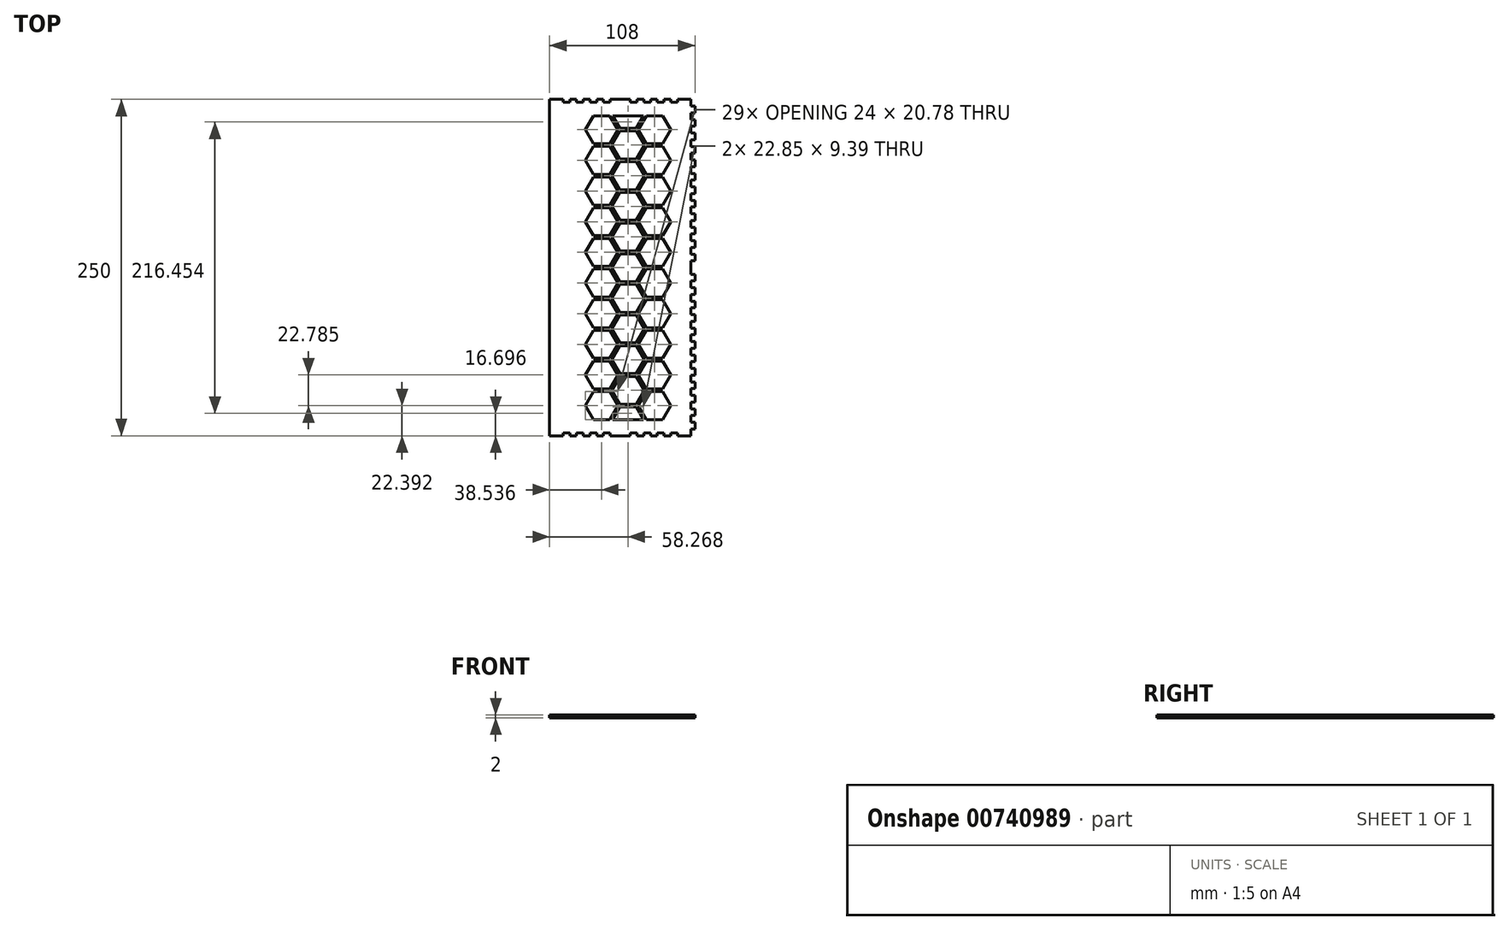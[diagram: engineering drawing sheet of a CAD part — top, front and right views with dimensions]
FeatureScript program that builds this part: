
annotation { "Feature Type Name" : "Feature", "Feature Type Description" : "" }
export const myFeature = defineFeature(function(context is Context, id is Id, definition is map)
    precondition{}
    {
        {
            var Q0;
            Q0=qCreatedBy(makeId("Top.planeOp"),FACE);
            var sketch = newSketch(context, id + "F0", { "sketchPlane" : qUnion([Q0])});
            skLineSegment(sketch, "E0.bottom", {"start": v(-52.5, 125) * mm, "end": v(-42.5, 125) * mm});
            skLineSegment(sketch, "E0.top", {"start": v(-52.5, -125) * mm, "end": v(-42.5, -125) * mm});
            skLineSegment(sketch, "E0.left", {"start": v(-52.5, 125) * mm, "end": v(-52.5, -125) * mm});
            skLineSegment(sketch, "E0.right", {"start": v(52.5, 125) * mm, "end": v(52.5, -125) * mm});
            skLineSegment(sketch, "E1", {"start": v(-52.5, 125) * mm, "end": v(52.5, -125) * mm, "construction": true});
            skLineSegment(sketch, "E2", {"start": v(52.5, 125) * mm, "end": v(-52.5, -125) * mm, "construction": true});
            skLineSegment(sketch, "E3.right", {"start": v(52.5, -126.05) * mm, "end": v(52.5, -119.95) * mm});
            skLineSegment(sketch, "E4.bottom", {"start": v(55.5, -45.05) * mm, "end": v(55.5, -49.95) * mm});
            skLineSegment(sketch, "E4.left", {"start": v(55.5, -45.05) * mm, "end": v(52.5, -45.05) * mm});
            skLineSegment(sketch, "E4.right", {"start": v(55.5, -49.95) * mm, "end": v(52.5, -49.95) * mm});
            skLineSegment(sketch, "E5.bottom", {"start": v(55.5, -55.05) * mm, "end": v(55.5, -59.95) * mm});
            skLineSegment(sketch, "E5.left", {"start": v(55.5, -55.05) * mm, "end": v(52.5, -55.05) * mm});
            skLineSegment(sketch, "E5.right", {"start": v(55.5, -59.95) * mm, "end": v(52.5, -59.95) * mm});
            skLineSegment(sketch, "E6.bottom", {"start": v(55.5, -65.05) * mm, "end": v(55.5, -69.95) * mm});
            skLineSegment(sketch, "E6.left", {"start": v(55.5, -65.05) * mm, "end": v(52.5, -65.05) * mm});
            skLineSegment(sketch, "E6.right", {"start": v(55.5, -69.95) * mm, "end": v(52.5, -69.95) * mm});
            skLineSegment(sketch, "E7.bottom", {"start": v(55.5, -75.05) * mm, "end": v(55.5, -79.95) * mm});
            skLineSegment(sketch, "E7.left", {"start": v(55.5, -75.05) * mm, "end": v(52.5, -75.05) * mm});
            skLineSegment(sketch, "E7.right", {"start": v(55.5, -79.95) * mm, "end": v(52.5, -79.95) * mm});
            skLineSegment(sketch, "E8.bottom", {"start": v(55.5, -85.05) * mm, "end": v(55.5, -89.95) * mm});
            skLineSegment(sketch, "E8.left", {"start": v(55.5, -85.05) * mm, "end": v(52.5, -85.05) * mm});
            skLineSegment(sketch, "E8.right", {"start": v(55.5, -89.95) * mm, "end": v(52.5, -89.95) * mm});
            skLineSegment(sketch, "E9.bottom", {"start": v(55.5, -95.05) * mm, "end": v(55.5, -99.95) * mm});
            skLineSegment(sketch, "E9.left", {"start": v(55.5, -95.05) * mm, "end": v(52.5, -95.05) * mm});
            skLineSegment(sketch, "E9.right", {"start": v(55.5, -99.95) * mm, "end": v(52.5, -99.95) * mm});
            skLineSegment(sketch, "E10.bottom", {"start": v(55.5, -105.05) * mm, "end": v(55.5, -109.95) * mm});
            skLineSegment(sketch, "E10.left", {"start": v(55.5, -105.05) * mm, "end": v(52.5, -105.05) * mm});
            skLineSegment(sketch, "E10.right", {"start": v(55.5, -109.95) * mm, "end": v(52.5, -109.95) * mm});
            skLineSegment(sketch, "E11.bottom", {"start": v(55.5, -115.05) * mm, "end": v(55.5, -119.95) * mm});
            skLineSegment(sketch, "E11.left", {"start": v(55.5, -115.05) * mm, "end": v(52.5, -115.05) * mm});
            skLineSegment(sketch, "E11.right", {"start": v(55.5, -119.95) * mm, "end": v(52.5, -119.95) * mm});
            skLineSegment(sketch, "E12.bottom", {"start": v(55.5, -15.05) * mm, "end": v(55.5, -19.95) * mm});
            skLineSegment(sketch, "E12.left", {"start": v(55.5, -15.05) * mm, "end": v(52.5, -15.05) * mm});
            skLineSegment(sketch, "E12.right", {"start": v(55.5, -19.95) * mm, "end": v(52.5, -19.95) * mm});
            skLineSegment(sketch, "E13.bottom", {"start": v(55.5, -25.05) * mm, "end": v(55.5, -29.95) * mm});
            skLineSegment(sketch, "E13.left", {"start": v(55.5, -25.05) * mm, "end": v(52.5, -25.05) * mm});
            skLineSegment(sketch, "E13.right", {"start": v(55.5, -29.95) * mm, "end": v(52.5, -29.95) * mm});
            skLineSegment(sketch, "E14.bottom", {"start": v(55.5, -35.05) * mm, "end": v(55.5, -39.95) * mm});
            skLineSegment(sketch, "E14.left", {"start": v(55.5, -35.05) * mm, "end": v(52.5, -35.05) * mm});
            skLineSegment(sketch, "E14.right", {"start": v(55.5, -39.95) * mm, "end": v(52.5, -39.95) * mm});
            skLineSegment(sketch, "E15.bottom", {"start": v(55.5, 89.95) * mm, "end": v(55.5, 85.05) * mm});
            skLineSegment(sketch, "E15.left", {"start": v(55.5, 89.95) * mm, "end": v(52.5, 89.95) * mm});
            skLineSegment(sketch, "E15.right", {"start": v(55.5, 85.05) * mm, "end": v(52.5, 85.05) * mm});
            skLineSegment(sketch, "E16.bottom", {"start": v(55.5, 79.95) * mm, "end": v(55.5, 75.05) * mm});
            skLineSegment(sketch, "E16.left", {"start": v(55.5, 79.95) * mm, "end": v(52.5, 79.95) * mm});
            skLineSegment(sketch, "E16.right", {"start": v(55.5, 75.05) * mm, "end": v(52.5, 75.05) * mm});
            skLineSegment(sketch, "E17.bottom", {"start": v(55.5, 69.95) * mm, "end": v(55.5, 65.05) * mm});
            skLineSegment(sketch, "E17.left", {"start": v(55.5, 69.95) * mm, "end": v(52.5, 69.95) * mm});
            skLineSegment(sketch, "E17.right", {"start": v(55.5, 65.05) * mm, "end": v(52.5, 65.05) * mm});
            skLineSegment(sketch, "E18.bottom", {"start": v(55.5, 59.95) * mm, "end": v(55.5, 55.05) * mm});
            skLineSegment(sketch, "E18.left", {"start": v(55.5, 59.95) * mm, "end": v(52.5, 59.95) * mm});
            skLineSegment(sketch, "E18.right", {"start": v(55.5, 55.05) * mm, "end": v(52.5, 55.05) * mm});
            skLineSegment(sketch, "E19.bottom", {"start": v(55.5, 49.95) * mm, "end": v(55.5, 45.05) * mm});
            skLineSegment(sketch, "E19.left", {"start": v(55.5, 49.95) * mm, "end": v(52.5, 49.95) * mm});
            skLineSegment(sketch, "E19.right", {"start": v(55.5, 45.05) * mm, "end": v(52.5, 45.05) * mm});
            skLineSegment(sketch, "E20.bottom", {"start": v(55.5, 39.95) * mm, "end": v(55.5, 35.05) * mm});
            skLineSegment(sketch, "E20.left", {"start": v(55.5, 39.95) * mm, "end": v(52.5, 39.95) * mm});
            skLineSegment(sketch, "E20.right", {"start": v(55.5, 35.05) * mm, "end": v(52.5, 35.05) * mm});
            skLineSegment(sketch, "E21.bottom", {"start": v(55.5, 29.95) * mm, "end": v(55.5, 25.05) * mm});
            skLineSegment(sketch, "E21.left", {"start": v(55.5, 29.95) * mm, "end": v(52.5, 29.95) * mm});
            skLineSegment(sketch, "E21.right", {"start": v(55.5, 25.05) * mm, "end": v(52.5, 25.05) * mm});
            skLineSegment(sketch, "E22.bottom", {"start": v(55.5, 19.95) * mm, "end": v(55.5, 15.05) * mm});
            skLineSegment(sketch, "E22.left", {"start": v(55.5, 19.95) * mm, "end": v(52.5, 19.95) * mm});
            skLineSegment(sketch, "E22.right", {"start": v(55.5, 15.05) * mm, "end": v(52.5, 15.05) * mm});
            skLineSegment(sketch, "E23.bottom", {"start": v(55.5, 119.95) * mm, "end": v(55.5, 115.05) * mm});
            skLineSegment(sketch, "E23.left", {"start": v(55.5, 119.95) * mm, "end": v(52.5, 119.95) * mm});
            skLineSegment(sketch, "E23.right", {"start": v(55.5, 115.05) * mm, "end": v(52.5, 115.05) * mm});
            skLineSegment(sketch, "E24.bottom", {"start": v(55.5, 109.95) * mm, "end": v(55.5, 105.05) * mm});
            skLineSegment(sketch, "E24.left", {"start": v(55.5, 109.95) * mm, "end": v(52.5, 109.95) * mm});
            skLineSegment(sketch, "E24.right", {"start": v(55.5, 105.05) * mm, "end": v(52.5, 105.05) * mm});
            skLineSegment(sketch, "E25.bottom", {"start": v(55.5, 99.95) * mm, "end": v(55.5, 95.05) * mm});
            skLineSegment(sketch, "E25.left", {"start": v(55.5, 99.95) * mm, "end": v(52.5, 99.95) * mm});
            skLineSegment(sketch, "E25.right", {"start": v(55.5, 95.05) * mm, "end": v(52.5, 95.05) * mm});
            skLineSegment(sketch, "E26.bottom", {"start": v(55.5, 9.95) * mm, "end": v(55.5, 5.05) * mm});
            skLineSegment(sketch, "E26.left", {"start": v(55.5, 9.95) * mm, "end": v(52.5, 9.95) * mm});
            skLineSegment(sketch, "E26.right", {"start": v(55.5, 5.05) * mm, "end": v(52.5, 5.05) * mm});
            skLineSegment(sketch, "E27.bottom", {"start": v(55.5, -5.05) * mm, "end": v(55.5, -9.95) * mm});
            skLineSegment(sketch, "E27.left", {"start": v(55.5, -5.05) * mm, "end": v(52.5, -5.05) * mm});
            skLineSegment(sketch, "E27.right", {"start": v(55.5, -9.95) * mm, "end": v(52.5, -9.95) * mm});
            skLineSegment(sketch, "E28.trimOffspring", {"start": v(52.5, -115.05) * mm, "end": v(52.5, -109.95) * mm});
            skLineSegment(sketch, "E29.trimOffspring", {"start": v(52.5, -105.05) * mm, "end": v(52.5, -99.95) * mm});
            skLineSegment(sketch, "E30.trimOffspring", {"start": v(52.5, -95.05) * mm, "end": v(52.5, -89.95) * mm});
            skLineSegment(sketch, "E31.trimOffspring", {"start": v(52.5, -85.05) * mm, "end": v(52.5, -79.95) * mm});
            skLineSegment(sketch, "E32.trimOffspring", {"start": v(52.5, -75.05) * mm, "end": v(52.5, -69.95) * mm});
            skLineSegment(sketch, "E33.trimOffspring", {"start": v(52.5, -65.05) * mm, "end": v(52.5, -59.95) * mm});
            skLineSegment(sketch, "E34.trimOffspring", {"start": v(52.5, -55.05) * mm, "end": v(52.5, -49.95) * mm});
            skLineSegment(sketch, "E35.trimOffspring", {"start": v(52.5, -45.05) * mm, "end": v(52.5, -39.95) * mm});
            skLineSegment(sketch, "E36.trimOffspring", {"start": v(52.5, -35.05) * mm, "end": v(52.5, -29.95) * mm});
            skLineSegment(sketch, "E37.trimOffspring", {"start": v(52.5, -25.05) * mm, "end": v(52.5, -19.95) * mm});
            skLineSegment(sketch, "E38.trimOffspring", {"start": v(52.5, -15.05) * mm, "end": v(52.5, -9.95) * mm});
            skLineSegment(sketch, "E39.trimOffspring", {"start": v(52.5, -5.05) * mm, "end": v(52.5, 5.05) * mm});
            skLineSegment(sketch, "E40.trimOffspring", {"start": v(52.5, 9.95) * mm, "end": v(52.5, 15.05) * mm});
            skLineSegment(sketch, "E41.trimOffspring", {"start": v(52.5, 19.95) * mm, "end": v(52.5, 25.05) * mm});
            skLineSegment(sketch, "E42.trimOffspring", {"start": v(52.5, 29.95) * mm, "end": v(52.5, 35.05) * mm});
            skLineSegment(sketch, "E43.trimOffspring", {"start": v(52.5, 39.95) * mm, "end": v(52.5, 45.05) * mm});
            skLineSegment(sketch, "E44.trimOffspring", {"start": v(52.5, 49.95) * mm, "end": v(52.5, 55.05) * mm});
            skLineSegment(sketch, "E45.trimOffspring", {"start": v(52.5, 59.95) * mm, "end": v(52.5, 65.05) * mm});
            skLineSegment(sketch, "E46.trimOffspring", {"start": v(52.5, 69.95) * mm, "end": v(52.5, 75.05) * mm});
            skLineSegment(sketch, "E47.trimOffspring", {"start": v(52.5, 79.95) * mm, "end": v(52.5, 85.05) * mm});
            skLineSegment(sketch, "E48.trimOffspring", {"start": v(52.5, 89.95) * mm, "end": v(52.5, 95.05) * mm});
            skLineSegment(sketch, "E49.trimOffspring", {"start": v(52.5, 99.95) * mm, "end": v(52.5, 105.05) * mm});
            skLineSegment(sketch, "E50.trimOffspring", {"start": v(52.5, 109.95) * mm, "end": v(52.5, 115.05) * mm});
            skLineSegment(sketch, "E51.trimOffspring", {"start": v(52.5, 119.95) * mm, "end": v(52.5, 124.8) * mm});
            skLineSegment(sketch, "E52", {"start": v(55.5, 125) * mm, "end": v(55.5, -126.05) * mm, "construction": true});
            skLineSegment(sketch, "E53", {"start": v(52.5, -126.05) * mm, "end": v(90.96, -126.05) * mm, "construction": true});
            skLineSegment(sketch, "E54", {"start": v(52.5, 125) * mm, "end": v(74.67, 125) * mm, "construction": true});
            skLineSegment(sketch, "E55.top", {"start": v(-42.5, 123) * mm, "end": v(-37.5, 123) * mm});
            skLineSegment(sketch, "E55.left", {"start": v(-42.5, 125) * mm, "end": v(-42.5, 123) * mm});
            skLineSegment(sketch, "E55.right", {"start": v(-37.5, 125) * mm, "end": v(-37.5, 123) * mm});
            skLineSegment(sketch, "E56.top", {"start": v(-32.5, 123) * mm, "end": v(-27.5, 123) * mm});
            skLineSegment(sketch, "E56.left", {"start": v(-32.5, 125) * mm, "end": v(-32.5, 123) * mm});
            skLineSegment(sketch, "E56.right", {"start": v(-27.5, 125) * mm, "end": v(-27.5, 123) * mm});
            skLineSegment(sketch, "E57.top", {"start": v(-22.5, 123) * mm, "end": v(-17.5, 123) * mm});
            skLineSegment(sketch, "E57.left", {"start": v(-22.5, 125) * mm, "end": v(-22.5, 123) * mm});
            skLineSegment(sketch, "E57.right", {"start": v(-17.5, 125) * mm, "end": v(-17.5, 123) * mm});
            skLineSegment(sketch, "E58.top", {"start": v(-12.5, 123) * mm, "end": v(-7.5, 123) * mm});
            skLineSegment(sketch, "E58.left", {"start": v(-12.5, 125) * mm, "end": v(-12.5, 123) * mm});
            skLineSegment(sketch, "E58.right", {"start": v(-7.5, 125) * mm, "end": v(-7.5, 123) * mm});
            skLineSegment(sketch, "E59.top", {"start": v(7.5, 123) * mm, "end": v(12.5, 123) * mm});
            skLineSegment(sketch, "E59.left", {"start": v(7.5, 125) * mm, "end": v(7.5, 123) * mm});
            skLineSegment(sketch, "E59.right", {"start": v(12.5, 125) * mm, "end": v(12.5, 123) * mm});
            skLineSegment(sketch, "E60.top", {"start": v(17.5, 123) * mm, "end": v(22.5, 123) * mm});
            skLineSegment(sketch, "E60.left", {"start": v(17.5, 125) * mm, "end": v(17.5, 123) * mm});
            skLineSegment(sketch, "E60.right", {"start": v(22.5, 125) * mm, "end": v(22.5, 123) * mm});
            skLineSegment(sketch, "E61.top", {"start": v(27.5, 123) * mm, "end": v(32.5, 123) * mm});
            skLineSegment(sketch, "E61.left", {"start": v(27.5, 125) * mm, "end": v(27.5, 123) * mm});
            skLineSegment(sketch, "E61.right", {"start": v(32.5, 125) * mm, "end": v(32.5, 123) * mm});
            skLineSegment(sketch, "E62.top", {"start": v(37.5, 123) * mm, "end": v(42.5, 123) * mm});
            skLineSegment(sketch, "E62.left", {"start": v(37.5, 125) * mm, "end": v(37.5, 123) * mm});
            skLineSegment(sketch, "E62.right", {"start": v(42.5, 125) * mm, "end": v(42.5, 123) * mm});
            skLineSegment(sketch, "E63.trimOffspring", {"start": v(-37.5, 125) * mm, "end": v(-32.5, 125) * mm});
            skLineSegment(sketch, "E64.trimOffspring", {"start": v(-27.5, 125) * mm, "end": v(-22.5, 125) * mm});
            skLineSegment(sketch, "E65.trimOffspring", {"start": v(-17.5, 125) * mm, "end": v(-12.5, 125) * mm});
            skLineSegment(sketch, "E66.trimOffspring", {"start": v(-7.5, 125) * mm, "end": v(7.5, 125) * mm});
            skLineSegment(sketch, "E67.trimOffspring", {"start": v(12.5, 125) * mm, "end": v(17.5, 125) * mm});
            skLineSegment(sketch, "E68.trimOffspring", {"start": v(22.5, 125) * mm, "end": v(27.5, 125) * mm});
            skLineSegment(sketch, "E69.trimOffspring", {"start": v(32.5, 125) * mm, "end": v(37.5, 125) * mm});
            skLineSegment(sketch, "E70", {"start": v(-52.5, 123) * mm, "end": v(52.5, 123) * mm, "construction": true});
            skLineSegment(sketch, "E71.top", {"start": v(42.5, -123) * mm, "end": v(37.5, -123) * mm});
            skLineSegment(sketch, "E71.left", {"start": v(42.5, -125) * mm, "end": v(42.5, -123) * mm});
            skLineSegment(sketch, "E71.right", {"start": v(37.5, -125) * mm, "end": v(37.5, -123) * mm});
            skLineSegment(sketch, "E72.top", {"start": v(32.5, -123) * mm, "end": v(27.5, -123) * mm});
            skLineSegment(sketch, "E72.left", {"start": v(32.5, -125) * mm, "end": v(32.5, -123) * mm});
            skLineSegment(sketch, "E72.right", {"start": v(27.5, -125) * mm, "end": v(27.5, -123) * mm});
            skLineSegment(sketch, "E73.top", {"start": v(22.5, -123) * mm, "end": v(17.5, -123) * mm});
            skLineSegment(sketch, "E73.left", {"start": v(22.5, -125) * mm, "end": v(22.5, -123) * mm});
            skLineSegment(sketch, "E73.right", {"start": v(17.5, -125) * mm, "end": v(17.5, -123) * mm});
            skLineSegment(sketch, "E74.top", {"start": v(12.5, -123) * mm, "end": v(7.5, -123) * mm});
            skLineSegment(sketch, "E74.left", {"start": v(12.5, -125) * mm, "end": v(12.5, -123) * mm});
            skLineSegment(sketch, "E74.right", {"start": v(7.5, -125) * mm, "end": v(7.5, -123) * mm});
            skLineSegment(sketch, "E75.top", {"start": v(-7.5, -123) * mm, "end": v(-12.5, -123) * mm});
            skLineSegment(sketch, "E75.left", {"start": v(-7.5, -125) * mm, "end": v(-7.5, -123) * mm});
            skLineSegment(sketch, "E75.right", {"start": v(-12.5, -125) * mm, "end": v(-12.5, -123) * mm});
            skLineSegment(sketch, "E76.top", {"start": v(-17.5, -123) * mm, "end": v(-22.5, -123) * mm});
            skLineSegment(sketch, "E76.left", {"start": v(-17.5, -125) * mm, "end": v(-17.5, -123) * mm});
            skLineSegment(sketch, "E76.right", {"start": v(-22.5, -125) * mm, "end": v(-22.5, -123) * mm});
            skLineSegment(sketch, "E77.top", {"start": v(-27.5, -123) * mm, "end": v(-32.5, -123) * mm});
            skLineSegment(sketch, "E77.left", {"start": v(-27.5, -125) * mm, "end": v(-27.5, -123) * mm});
            skLineSegment(sketch, "E77.right", {"start": v(-32.5, -125) * mm, "end": v(-32.5, -123) * mm});
            skLineSegment(sketch, "E78.top", {"start": v(-37.5, -123) * mm, "end": v(-42.5, -123) * mm});
            skLineSegment(sketch, "E78.left", {"start": v(-37.5, -125) * mm, "end": v(-37.5, -123) * mm});
            skLineSegment(sketch, "E78.right", {"start": v(-42.5, -125) * mm, "end": v(-42.5, -123) * mm});
            skLineSegment(sketch, "E79.trimOffspring", {"start": v(37.5, -125) * mm, "end": v(32.5, -125) * mm});
            skLineSegment(sketch, "E80.trimOffspring", {"start": v(27.5, -125) * mm, "end": v(22.5, -125) * mm});
            skLineSegment(sketch, "E81.trimOffspring", {"start": v(17.5, -125) * mm, "end": v(12.5, -125) * mm});
            skLineSegment(sketch, "E82.trimOffspring", {"start": v(7.5, -125) * mm, "end": v(-7.5, -125) * mm});
            skLineSegment(sketch, "E83.trimOffspring", {"start": v(-12.5, -125) * mm, "end": v(-17.5, -125) * mm});
            skLineSegment(sketch, "E84.trimOffspring", {"start": v(-22.5, -125) * mm, "end": v(-27.5, -125) * mm});
            skLineSegment(sketch, "E85.trimOffspring", {"start": v(-32.5, -125) * mm, "end": v(-37.5, -125) * mm});
            skLineSegment(sketch, "E86", {"start": v(-52.5, -123) * mm, "end": v(52.5, -123) * mm, "construction": true});
            skLineSegment(sketch, "E87.trimOffspring", {"start": v(42.5, 125) * mm, "end": v(52.5, 125) * mm});
            skLineSegment(sketch, "E88.trimOffspring", {"start": v(-37.5, -125) * mm, "end": v(-32.5, -125) * mm});
            skLineSegment(sketch, "E89.trimOffspring", {"start": v(-17.5, -125) * mm, "end": v(-12.5, -125) * mm});
            skLineSegment(sketch, "E90.trimOffspring", {"start": v(-7.5, -125) * mm, "end": v(7.5, -125) * mm});
            skLineSegment(sketch, "E91.trimOffspring", {"start": v(12.5, -125) * mm, "end": v(17.5, -125) * mm});
            skLineSegment(sketch, "E92.trimOffspring", {"start": v(22.5, -125) * mm, "end": v(27.5, -125) * mm});
            skLineSegment(sketch, "E93.trimOffspring", {"start": v(32.5, -125) * mm, "end": v(37.5, -125) * mm});
            skLineSegment(sketch, "E94.trimOffspring", {"start": v(42.5, -125) * mm, "end": v(52.5, -125) * mm});
            skSolve(sketch);
        }
        {
            var Q0;
            Q0=makeQuery(id+"F0.imprint","IMPRINT",FACE,{"disambiguationData":[TD([[makeQuery(id+"F0.imprint","IMPRINT",EDGE,{"derivedFrom":sQuery(id+"F0.wireOp",EDGE,"E0.bottom")}),-1.0]])]});
            var sketch = newSketch(context, id + "F1", { "sketchPlane" : qUnion([Q0])});
            skLineSegment(sketch, "E95", {"start": v(-25.96, -113) * mm, "end": v(64.04, -113) * mm, "construction": true});
            skLineSegment(sketch, "E96", {"start": v(-25.96, -113) * mm, "end": v(-25.96, 147) * mm, "construction": true});
            skCircle(sketch, "E97.cCircle", {"center": v(-13.96, -102.6) * mm, "radius": 10.4 * mm, "construction": true});
            skLineSegment(sketch, "E97.0", {"start": v(-7.96, -92.22) * mm, "end": v(-1.96, -102.6) * mm});
            skLineSegment(sketch, "E97.1", {"start": v(-1.96, -102.6) * mm, "end": v(-7.96, -113) * mm});
            skLineSegment(sketch, "E97.2", {"start": v(-7.96, -113) * mm, "end": v(-19.96, -113) * mm});
            skLineSegment(sketch, "E97.3", {"start": v(-19.96, -113) * mm, "end": v(-25.96, -102.6) * mm});
            skLineSegment(sketch, "E97.4", {"start": v(-25.96, -102.6) * mm, "end": v(-19.96, -92.22) * mm});
            skLineSegment(sketch, "E97.5", {"start": v(-19.96, -92.22) * mm, "end": v(-7.96, -92.22) * mm});
            skPoint(sketch, "E97.0.midPoint", {"position": v(-4.96, -97.41) * mm});
            skCircle(sketch, "E98.cCircle", {"center": v(-13.96, -79.82) * mm, "radius": 10.4 * mm, "construction": true});
            skLineSegment(sketch, "E98.0", {"start": v(-7.96, -69.43) * mm, "end": v(-1.96, -79.82) * mm});
            skLineSegment(sketch, "E98.1", {"start": v(-1.96, -79.82) * mm, "end": v(-7.96, -90.22) * mm});
            skLineSegment(sketch, "E98.2", {"start": v(-7.96, -90.22) * mm, "end": v(-19.96, -90.22) * mm});
            skLineSegment(sketch, "E98.3", {"start": v(-19.96, -90.22) * mm, "end": v(-25.96, -79.82) * mm});
            skLineSegment(sketch, "E98.4", {"start": v(-25.96, -79.82) * mm, "end": v(-19.96, -69.43) * mm});
            skLineSegment(sketch, "E98.5", {"start": v(-19.96, -69.43) * mm, "end": v(-7.96, -69.43) * mm});
            skPoint(sketch, "E98.0.midPoint", {"position": v(-4.96, -74.63) * mm});
            skCircle(sketch, "E99.cCircle", {"center": v(-13.96, -57.04) * mm, "radius": 10.4 * mm, "construction": true});
            skLineSegment(sketch, "E99.0", {"start": v(-7.96, -46.65) * mm, "end": v(-1.96, -57.04) * mm});
            skLineSegment(sketch, "E99.1", {"start": v(-1.96, -57.04) * mm, "end": v(-7.96, -67.43) * mm});
            skLineSegment(sketch, "E99.2", {"start": v(-7.96, -67.43) * mm, "end": v(-19.96, -67.43) * mm});
            skLineSegment(sketch, "E99.3", {"start": v(-19.96, -67.43) * mm, "end": v(-25.96, -57.04) * mm});
            skLineSegment(sketch, "E99.4", {"start": v(-25.96, -57.04) * mm, "end": v(-19.96, -46.65) * mm});
            skLineSegment(sketch, "E99.5", {"start": v(-19.96, -46.65) * mm, "end": v(-7.96, -46.65) * mm});
            skPoint(sketch, "E99.0.midPoint", {"position": v(-4.96, -51.84) * mm});
            skCircle(sketch, "E100.cCircle", {"center": v(-13.96, -34.25) * mm, "radius": 10.4 * mm, "construction": true});
            skLineSegment(sketch, "E100.0", {"start": v(-7.96, -23.86) * mm, "end": v(-1.96, -34.25) * mm});
            skLineSegment(sketch, "E100.1", {"start": v(-1.96, -34.25) * mm, "end": v(-7.96, -44.65) * mm});
            skLineSegment(sketch, "E100.2", {"start": v(-7.96, -44.65) * mm, "end": v(-19.96, -44.65) * mm});
            skLineSegment(sketch, "E100.3", {"start": v(-19.96, -44.65) * mm, "end": v(-25.96, -34.25) * mm});
            skLineSegment(sketch, "E100.4", {"start": v(-25.96, -34.25) * mm, "end": v(-19.96, -23.86) * mm});
            skLineSegment(sketch, "E100.5", {"start": v(-19.96, -23.86) * mm, "end": v(-7.96, -23.86) * mm});
            skPoint(sketch, "E100.0.midPoint", {"position": v(-4.96, -29.06) * mm});
            skCircle(sketch, "E101.cCircle", {"center": v(-13.96, -11.47) * mm, "radius": 10.4 * mm, "construction": true});
            skLineSegment(sketch, "E101.0", {"start": v(-7.96, -1.08) * mm, "end": v(-1.96, -11.47) * mm});
            skLineSegment(sketch, "E101.1", {"start": v(-1.96, -11.47) * mm, "end": v(-7.96, -21.86) * mm});
            skLineSegment(sketch, "E101.2", {"start": v(-7.96, -21.86) * mm, "end": v(-19.96, -21.86) * mm});
            skLineSegment(sketch, "E101.3", {"start": v(-19.96, -21.86) * mm, "end": v(-25.96, -11.47) * mm});
            skLineSegment(sketch, "E101.4", {"start": v(-25.96, -11.47) * mm, "end": v(-19.96, -1.08) * mm});
            skLineSegment(sketch, "E101.5", {"start": v(-19.96, -1.08) * mm, "end": v(-7.96, -1.08) * mm});
            skPoint(sketch, "E101.0.midPoint", {"position": v(-4.96, -6.27) * mm});
            skCircle(sketch, "E102.cCircle", {"center": v(-13.96, 11.32) * mm, "radius": 10.4 * mm, "construction": true});
            skLineSegment(sketch, "E102.0", {"start": v(-7.96, 21.7) * mm, "end": v(-1.96, 11.32) * mm});
            skLineSegment(sketch, "E102.1", {"start": v(-1.96, 11.32) * mm, "end": v(-7.96, 0.92) * mm});
            skLineSegment(sketch, "E102.2", {"start": v(-7.96, 0.92) * mm, "end": v(-19.96, 0.92) * mm});
            skLineSegment(sketch, "E102.3", {"start": v(-19.96, 0.92) * mm, "end": v(-25.96, 11.32) * mm});
            skLineSegment(sketch, "E102.4", {"start": v(-25.96, 11.32) * mm, "end": v(-19.96, 21.7) * mm});
            skLineSegment(sketch, "E102.5", {"start": v(-19.96, 21.7) * mm, "end": v(-7.96, 21.7) * mm});
            skPoint(sketch, "E102.0.midPoint", {"position": v(-4.96, 16.51) * mm});
            skCircle(sketch, "E103.cCircle", {"center": v(-13.96, 34.1) * mm, "radius": 10.4 * mm, "construction": true});
            skLineSegment(sketch, "E103.0", {"start": v(-7.96, 44.5) * mm, "end": v(-1.96, 34.1) * mm});
            skLineSegment(sketch, "E103.1", {"start": v(-1.96, 34.1) * mm, "end": v(-7.96, 23.7) * mm});
            skLineSegment(sketch, "E103.2", {"start": v(-7.96, 23.7) * mm, "end": v(-19.96, 23.7) * mm});
            skLineSegment(sketch, "E103.3", {"start": v(-19.96, 23.7) * mm, "end": v(-25.96, 34.1) * mm});
            skLineSegment(sketch, "E103.4", {"start": v(-25.96, 34.1) * mm, "end": v(-19.96, 44.5) * mm});
            skLineSegment(sketch, "E103.5", {"start": v(-19.96, 44.5) * mm, "end": v(-7.96, 44.5) * mm});
            skPoint(sketch, "E103.0.midPoint", {"position": v(-4.96, 39.3) * mm});
            skCircle(sketch, "E104.cCircle", {"center": v(-13.96, 56.88) * mm, "radius": 10.4 * mm, "construction": true});
            skLineSegment(sketch, "E104.0", {"start": v(-7.96, 67.28) * mm, "end": v(-1.96, 56.88) * mm});
            skLineSegment(sketch, "E104.1", {"start": v(-1.96, 56.88) * mm, "end": v(-7.96, 46.5) * mm});
            skLineSegment(sketch, "E104.2", {"start": v(-7.96, 46.5) * mm, "end": v(-19.96, 46.5) * mm});
            skLineSegment(sketch, "E104.3", {"start": v(-19.96, 46.5) * mm, "end": v(-25.96, 56.88) * mm});
            skLineSegment(sketch, "E104.4", {"start": v(-25.96, 56.88) * mm, "end": v(-19.96, 67.28) * mm});
            skLineSegment(sketch, "E104.5", {"start": v(-19.96, 67.28) * mm, "end": v(-7.96, 67.28) * mm});
            skPoint(sketch, "E104.0.midPoint", {"position": v(-4.96, 62.08) * mm});
            skCircle(sketch, "E105.cCircle", {"center": v(-13.96, 79.67) * mm, "radius": 10.4 * mm, "construction": true});
            skLineSegment(sketch, "E105.0", {"start": v(-7.96, 90.06) * mm, "end": v(-1.96, 79.67) * mm});
            skLineSegment(sketch, "E105.1", {"start": v(-1.96, 79.67) * mm, "end": v(-7.96, 69.28) * mm});
            skLineSegment(sketch, "E105.2", {"start": v(-7.96, 69.28) * mm, "end": v(-19.96, 69.28) * mm});
            skLineSegment(sketch, "E105.3", {"start": v(-19.96, 69.28) * mm, "end": v(-25.96, 79.67) * mm});
            skLineSegment(sketch, "E105.4", {"start": v(-25.96, 79.67) * mm, "end": v(-19.96, 90.06) * mm});
            skLineSegment(sketch, "E105.5", {"start": v(-19.96, 90.06) * mm, "end": v(-7.96, 90.06) * mm});
            skPoint(sketch, "E105.0.midPoint", {"position": v(-4.96, 84.87) * mm});
            skCircle(sketch, "E106.cCircle", {"center": v(-13.96, 102.45) * mm, "radius": 10.4 * mm, "construction": true});
            skLineSegment(sketch, "E106.0", {"start": v(-7.96, 112.85) * mm, "end": v(-1.96, 102.45) * mm});
            skLineSegment(sketch, "E106.1", {"start": v(-1.96, 102.45) * mm, "end": v(-7.96, 92.06) * mm});
            skLineSegment(sketch, "E106.2", {"start": v(-7.96, 92.06) * mm, "end": v(-19.96, 92.06) * mm});
            skLineSegment(sketch, "E106.3", {"start": v(-19.96, 92.06) * mm, "end": v(-25.96, 102.45) * mm});
            skLineSegment(sketch, "E106.4", {"start": v(-25.96, 102.45) * mm, "end": v(-19.96, 112.85) * mm});
            skLineSegment(sketch, "E106.5", {"start": v(-19.96, 112.85) * mm, "end": v(-7.96, 112.85) * mm});
            skPoint(sketch, "E106.0.midPoint", {"position": v(-4.96, 107.65) * mm});
            skArc(sketch, "E107.cCircle", {"start": v(16.11, -113) * mm, "mid": v(5.77, -103.6) * mm, "end": v(-4.58, -113) * mm, "construction": true});
            skLineSegment(sketch, "E107.0", {"start": v(11.77, -103.6) * mm, "end": v(17.2, -113) * mm});
            skLineSegment(sketch, "E107.4", {"start": v(-5.65, -113) * mm, "end": v(-0.23, -103.6) * mm});
            skLineSegment(sketch, "E107.5", {"start": v(-0.23, -103.6) * mm, "end": v(11.77, -103.6) * mm});
            skPoint(sketch, "E107.0.midPoint", {"position": v(14.77, -108.8) * mm});
            skCircle(sketch, "E108.cCircle", {"center": v(5.77, -68.43) * mm, "radius": 10.4 * mm, "construction": true});
            skLineSegment(sketch, "E108.0", {"start": v(11.77, -58.04) * mm, "end": v(17.77, -68.43) * mm});
            skLineSegment(sketch, "E108.1", {"start": v(17.77, -68.43) * mm, "end": v(11.77, -78.82) * mm});
            skLineSegment(sketch, "E108.2", {"start": v(11.77, -78.82) * mm, "end": v(-0.23, -78.82) * mm});
            skLineSegment(sketch, "E108.3", {"start": v(-0.23, -78.82) * mm, "end": v(-6.23, -68.43) * mm});
            skLineSegment(sketch, "E108.4", {"start": v(-6.23, -68.43) * mm, "end": v(-0.23, -58.04) * mm});
            skLineSegment(sketch, "E108.5", {"start": v(-0.23, -58.04) * mm, "end": v(11.77, -58.04) * mm});
            skPoint(sketch, "E108.0.midPoint", {"position": v(14.77, -63.23) * mm});
            skCircle(sketch, "E109.cCircle", {"center": v(5.77, -45.65) * mm, "radius": 10.4 * mm, "construction": true});
            skLineSegment(sketch, "E109.0", {"start": v(11.77, -35.25) * mm, "end": v(17.77, -45.65) * mm});
            skLineSegment(sketch, "E109.1", {"start": v(17.77, -45.65) * mm, "end": v(11.77, -56.04) * mm});
            skLineSegment(sketch, "E109.2", {"start": v(11.77, -56.04) * mm, "end": v(-0.23, -56.04) * mm});
            skLineSegment(sketch, "E109.3", {"start": v(-0.23, -56.04) * mm, "end": v(-6.23, -45.65) * mm});
            skLineSegment(sketch, "E109.4", {"start": v(-6.23, -45.65) * mm, "end": v(-0.23, -35.25) * mm});
            skLineSegment(sketch, "E109.5", {"start": v(-0.23, -35.25) * mm, "end": v(11.77, -35.25) * mm});
            skPoint(sketch, "E109.0.midPoint", {"position": v(14.77, -40.45) * mm});
            skCircle(sketch, "E110.cCircle", {"center": v(5.77, -22.86) * mm, "radius": 10.4 * mm, "construction": true});
            skLineSegment(sketch, "E110.0", {"start": v(11.77, -12.47) * mm, "end": v(17.77, -22.86) * mm});
            skLineSegment(sketch, "E110.1", {"start": v(17.77, -22.86) * mm, "end": v(11.77, -33.25) * mm});
            skLineSegment(sketch, "E110.2", {"start": v(11.77, -33.25) * mm, "end": v(-0.23, -33.25) * mm});
            skLineSegment(sketch, "E110.3", {"start": v(-0.23, -33.25) * mm, "end": v(-6.23, -22.86) * mm});
            skLineSegment(sketch, "E110.4", {"start": v(-6.23, -22.86) * mm, "end": v(-0.23, -12.47) * mm});
            skLineSegment(sketch, "E110.5", {"start": v(-0.23, -12.47) * mm, "end": v(11.77, -12.47) * mm});
            skPoint(sketch, "E110.0.midPoint", {"position": v(14.77, -17.67) * mm});
            skCircle(sketch, "E111.cCircle", {"center": v(5.77, -0.08) * mm, "radius": 10.4 * mm, "construction": true});
            skLineSegment(sketch, "E111.0", {"start": v(11.77, 10.32) * mm, "end": v(17.77, -0.08) * mm});
            skLineSegment(sketch, "E111.1", {"start": v(17.77, -0.08) * mm, "end": v(11.77, -10.47) * mm});
            skLineSegment(sketch, "E111.2", {"start": v(11.77, -10.47) * mm, "end": v(-0.23, -10.47) * mm});
            skLineSegment(sketch, "E111.3", {"start": v(-0.23, -10.47) * mm, "end": v(-6.23, -0.08) * mm});
            skLineSegment(sketch, "E111.4", {"start": v(-6.23, -0.08) * mm, "end": v(-0.23, 10.32) * mm});
            skLineSegment(sketch, "E111.5", {"start": v(-0.23, 10.32) * mm, "end": v(11.77, 10.32) * mm});
            skPoint(sketch, "E111.0.midPoint", {"position": v(14.77, 5.12) * mm});
            skCircle(sketch, "E112.cCircle", {"center": v(5.77, 22.7) * mm, "radius": 10.4 * mm, "construction": true});
            skLineSegment(sketch, "E112.0", {"start": v(11.77, 33.1) * mm, "end": v(17.77, 22.7) * mm});
            skLineSegment(sketch, "E112.1", {"start": v(17.77, 22.7) * mm, "end": v(11.77, 12.32) * mm});
            skLineSegment(sketch, "E112.2", {"start": v(11.77, 12.32) * mm, "end": v(-0.23, 12.32) * mm});
            skLineSegment(sketch, "E112.3", {"start": v(-0.23, 12.32) * mm, "end": v(-6.23, 22.7) * mm});
            skLineSegment(sketch, "E112.4", {"start": v(-6.23, 22.7) * mm, "end": v(-0.23, 33.1) * mm});
            skLineSegment(sketch, "E112.5", {"start": v(-0.23, 33.1) * mm, "end": v(11.77, 33.1) * mm});
            skPoint(sketch, "E112.0.midPoint", {"position": v(14.77, 27.9) * mm});
            skCircle(sketch, "E113.cCircle", {"center": v(5.77, 45.5) * mm, "radius": 10.4 * mm, "construction": true});
            skLineSegment(sketch, "E113.0", {"start": v(11.77, 55.88) * mm, "end": v(17.77, 45.5) * mm});
            skLineSegment(sketch, "E113.1", {"start": v(17.77, 45.5) * mm, "end": v(11.77, 35.1) * mm});
            skLineSegment(sketch, "E113.2", {"start": v(11.77, 35.1) * mm, "end": v(-0.23, 35.1) * mm});
            skLineSegment(sketch, "E113.3", {"start": v(-0.23, 35.1) * mm, "end": v(-6.23, 45.5) * mm});
            skLineSegment(sketch, "E113.4", {"start": v(-6.23, 45.5) * mm, "end": v(-0.23, 55.88) * mm});
            skLineSegment(sketch, "E113.5", {"start": v(-0.23, 55.88) * mm, "end": v(11.77, 55.88) * mm});
            skPoint(sketch, "E113.0.midPoint", {"position": v(14.77, 50.69) * mm});
            skCircle(sketch, "E114.cCircle", {"center": v(5.77, 68.28) * mm, "radius": 10.4 * mm, "construction": true});
            skLineSegment(sketch, "E114.0", {"start": v(11.77, 78.67) * mm, "end": v(17.77, 68.28) * mm});
            skLineSegment(sketch, "E114.1", {"start": v(17.77, 68.28) * mm, "end": v(11.77, 57.88) * mm});
            skLineSegment(sketch, "E114.2", {"start": v(11.77, 57.88) * mm, "end": v(-0.23, 57.88) * mm});
            skLineSegment(sketch, "E114.3", {"start": v(-0.23, 57.88) * mm, "end": v(-6.23, 68.28) * mm});
            skLineSegment(sketch, "E114.4", {"start": v(-6.23, 68.28) * mm, "end": v(-0.23, 78.67) * mm});
            skLineSegment(sketch, "E114.5", {"start": v(-0.23, 78.67) * mm, "end": v(11.77, 78.67) * mm});
            skPoint(sketch, "E114.0.midPoint", {"position": v(14.77, 73.47) * mm});
            skCircle(sketch, "E115.cCircle", {"center": v(5.77, 91.06) * mm, "radius": 10.4 * mm, "construction": true});
            skLineSegment(sketch, "E115.0", {"start": v(11.77, 101.45) * mm, "end": v(17.77, 91.06) * mm});
            skLineSegment(sketch, "E115.1", {"start": v(17.77, 91.06) * mm, "end": v(11.77, 80.67) * mm});
            skLineSegment(sketch, "E115.2", {"start": v(11.77, 80.67) * mm, "end": v(-0.23, 80.67) * mm});
            skLineSegment(sketch, "E115.3", {"start": v(-0.23, 80.67) * mm, "end": v(-6.23, 91.06) * mm});
            skLineSegment(sketch, "E115.4", {"start": v(-6.23, 91.06) * mm, "end": v(-0.23, 101.45) * mm});
            skLineSegment(sketch, "E115.5", {"start": v(-0.23, 101.45) * mm, "end": v(11.77, 101.45) * mm});
            skPoint(sketch, "E115.0.midPoint", {"position": v(14.77, 96.26) * mm});
            skLineSegment(sketch, "E116", {"start": v(-6.23, 147) * mm, "end": v(-6.23, -113) * mm, "construction": true});
            skCircle(sketch, "E117.cCircle", {"center": v(5.77, -91.22) * mm, "radius": 10.4 * mm, "construction": true});
            skLineSegment(sketch, "E117.0", {"start": v(11.77, -80.82) * mm, "end": v(17.77, -91.22) * mm});
            skLineSegment(sketch, "E117.1", {"start": v(17.77, -91.22) * mm, "end": v(11.77, -101.6) * mm});
            skLineSegment(sketch, "E117.2", {"start": v(11.77, -101.6) * mm, "end": v(-0.23, -101.6) * mm});
            skLineSegment(sketch, "E117.3", {"start": v(-0.23, -101.6) * mm, "end": v(-6.23, -91.22) * mm});
            skLineSegment(sketch, "E117.4", {"start": v(-6.23, -91.22) * mm, "end": v(-0.23, -80.82) * mm});
            skLineSegment(sketch, "E117.5", {"start": v(-0.23, -80.82) * mm, "end": v(11.77, -80.82) * mm});
            skPoint(sketch, "E117.0.midPoint", {"position": v(14.77, -86.02) * mm});
            skLineSegment(sketch, "E118", {"start": v(17.77, -117) * mm, "end": v(17.77, 148.22) * mm, "construction": true});
            skArc(sketch, "E119.cCircle", {"start": v(-4.59, 113) * mm, "mid": v(5.77, 103.45) * mm, "end": v(16.13, 113) * mm, "construction": true});
            skLineSegment(sketch, "E119.1", {"start": v(17.2, 112.85) * mm, "end": v(11.77, 103.45) * mm});
            skLineSegment(sketch, "E119.2", {"start": v(11.77, 103.45) * mm, "end": v(-0.23, 103.45) * mm});
            skLineSegment(sketch, "E119.3", {"start": v(-0.23, 103.45) * mm, "end": v(-5.65, 112.85) * mm});
            skPoint(sketch, "E119.0.midPoint", {"position": v(14.77, 119.04) * mm});
            skCircle(sketch, "E120.cCircle", {"center": v(25.5, -102.6) * mm, "radius": 10.4 * mm, "construction": true});
            skLineSegment(sketch, "E120.0", {"start": v(31.5, -92.22) * mm, "end": v(37.5, -102.6) * mm});
            skLineSegment(sketch, "E120.1", {"start": v(37.5, -102.6) * mm, "end": v(31.5, -113) * mm});
            skLineSegment(sketch, "E120.2", {"start": v(31.5, -113) * mm, "end": v(19.5, -113) * mm});
            skLineSegment(sketch, "E120.3", {"start": v(19.5, -113) * mm, "end": v(13.5, -102.6) * mm});
            skLineSegment(sketch, "E120.4", {"start": v(13.5, -102.6) * mm, "end": v(19.5, -92.22) * mm});
            skLineSegment(sketch, "E120.5", {"start": v(19.5, -92.22) * mm, "end": v(31.5, -92.22) * mm});
            skPoint(sketch, "E120.0.midPoint", {"position": v(34.5, -97.41) * mm});
            skLineSegment(sketch, "E121", {"start": v(13.5, -113) * mm, "end": v(13.5, 147) * mm, "construction": true});
            skLineSegment(sketch, "E122", {"start": v(37.5, -113) * mm, "end": v(37.5, 147) * mm, "construction": true});
            skCircle(sketch, "E123.cCircle", {"center": v(25.5, -79.82) * mm, "radius": 10.4 * mm, "construction": true});
            skLineSegment(sketch, "E123.0", {"start": v(31.5, -69.43) * mm, "end": v(37.5, -79.82) * mm});
            skLineSegment(sketch, "E123.1", {"start": v(37.5, -79.82) * mm, "end": v(31.5, -90.22) * mm});
            skLineSegment(sketch, "E123.2", {"start": v(31.5, -90.22) * mm, "end": v(19.5, -90.22) * mm});
            skLineSegment(sketch, "E123.3", {"start": v(19.5, -90.22) * mm, "end": v(13.5, -79.82) * mm});
            skLineSegment(sketch, "E123.4", {"start": v(13.5, -79.82) * mm, "end": v(19.5, -69.43) * mm});
            skLineSegment(sketch, "E123.5", {"start": v(19.5, -69.43) * mm, "end": v(31.5, -69.43) * mm});
            skPoint(sketch, "E123.0.midPoint", {"position": v(34.5, -74.63) * mm});
            skCircle(sketch, "E124.cCircle", {"center": v(25.5, -57.04) * mm, "radius": 10.4 * mm, "construction": true});
            skLineSegment(sketch, "E124.0", {"start": v(31.5, -46.65) * mm, "end": v(37.5, -57.04) * mm});
            skLineSegment(sketch, "E124.1", {"start": v(37.5, -57.04) * mm, "end": v(31.5, -67.43) * mm});
            skLineSegment(sketch, "E124.2", {"start": v(31.5, -67.43) * mm, "end": v(19.5, -67.43) * mm});
            skLineSegment(sketch, "E124.3", {"start": v(19.5, -67.43) * mm, "end": v(13.5, -57.04) * mm});
            skLineSegment(sketch, "E124.4", {"start": v(13.5, -57.04) * mm, "end": v(19.5, -46.65) * mm});
            skLineSegment(sketch, "E124.5", {"start": v(19.5, -46.65) * mm, "end": v(31.5, -46.65) * mm});
            skPoint(sketch, "E124.0.midPoint", {"position": v(34.5, -51.84) * mm});
            skCircle(sketch, "E125.cCircle", {"center": v(25.5, -34.25) * mm, "radius": 10.4 * mm, "construction": true});
            skLineSegment(sketch, "E125.0", {"start": v(31.5, -23.86) * mm, "end": v(37.5, -34.25) * mm});
            skLineSegment(sketch, "E125.1", {"start": v(37.5, -34.25) * mm, "end": v(31.5, -44.65) * mm});
            skLineSegment(sketch, "E125.2", {"start": v(31.5, -44.65) * mm, "end": v(19.5, -44.65) * mm});
            skLineSegment(sketch, "E125.3", {"start": v(19.5, -44.65) * mm, "end": v(13.5, -34.25) * mm});
            skLineSegment(sketch, "E125.4", {"start": v(13.5, -34.25) * mm, "end": v(19.5, -23.86) * mm});
            skLineSegment(sketch, "E125.5", {"start": v(19.5, -23.86) * mm, "end": v(31.5, -23.86) * mm});
            skPoint(sketch, "E125.0.midPoint", {"position": v(34.5, -29.06) * mm});
            skCircle(sketch, "E126.cCircle", {"center": v(25.5, -11.47) * mm, "radius": 10.4 * mm, "construction": true});
            skLineSegment(sketch, "E126.0", {"start": v(31.5, -1.08) * mm, "end": v(37.5, -11.47) * mm});
            skLineSegment(sketch, "E126.1", {"start": v(37.5, -11.47) * mm, "end": v(31.5, -21.86) * mm});
            skLineSegment(sketch, "E126.2", {"start": v(31.5, -21.86) * mm, "end": v(19.5, -21.86) * mm});
            skLineSegment(sketch, "E126.3", {"start": v(19.5, -21.86) * mm, "end": v(13.5, -11.47) * mm});
            skLineSegment(sketch, "E126.4", {"start": v(13.5, -11.47) * mm, "end": v(19.5, -1.08) * mm});
            skLineSegment(sketch, "E126.5", {"start": v(19.5, -1.08) * mm, "end": v(31.5, -1.08) * mm});
            skPoint(sketch, "E126.0.midPoint", {"position": v(34.5, -6.27) * mm});
            skCircle(sketch, "E127.cCircle", {"center": v(25.5, 11.32) * mm, "radius": 10.4 * mm, "construction": true});
            skLineSegment(sketch, "E127.0", {"start": v(31.5, 21.7) * mm, "end": v(37.5, 11.32) * mm});
            skLineSegment(sketch, "E127.1", {"start": v(37.5, 11.32) * mm, "end": v(31.5, 0.92) * mm});
            skLineSegment(sketch, "E127.2", {"start": v(31.5, 0.92) * mm, "end": v(19.5, 0.92) * mm});
            skLineSegment(sketch, "E127.3", {"start": v(19.5, 0.92) * mm, "end": v(13.5, 11.32) * mm});
            skLineSegment(sketch, "E127.4", {"start": v(13.5, 11.32) * mm, "end": v(19.5, 21.7) * mm});
            skLineSegment(sketch, "E127.5", {"start": v(19.5, 21.7) * mm, "end": v(31.5, 21.7) * mm});
            skPoint(sketch, "E127.0.midPoint", {"position": v(34.5, 16.51) * mm});
            skCircle(sketch, "E128.cCircle", {"center": v(25.5, 34.1) * mm, "radius": 10.4 * mm, "construction": true});
            skLineSegment(sketch, "E128.0", {"start": v(31.5, 44.5) * mm, "end": v(37.5, 34.1) * mm});
            skLineSegment(sketch, "E128.1", {"start": v(37.5, 34.1) * mm, "end": v(31.5, 23.7) * mm});
            skLineSegment(sketch, "E128.2", {"start": v(31.5, 23.7) * mm, "end": v(19.5, 23.7) * mm});
            skLineSegment(sketch, "E128.3", {"start": v(19.5, 23.7) * mm, "end": v(13.5, 34.1) * mm});
            skLineSegment(sketch, "E128.4", {"start": v(13.5, 34.1) * mm, "end": v(19.5, 44.5) * mm});
            skLineSegment(sketch, "E128.5", {"start": v(19.5, 44.5) * mm, "end": v(31.5, 44.5) * mm});
            skPoint(sketch, "E128.0.midPoint", {"position": v(34.5, 39.3) * mm});
            skCircle(sketch, "E129.cCircle", {"center": v(25.5, 56.88) * mm, "radius": 10.4 * mm, "construction": true});
            skLineSegment(sketch, "E129.0", {"start": v(31.5, 67.28) * mm, "end": v(37.5, 56.88) * mm});
            skLineSegment(sketch, "E129.1", {"start": v(37.5, 56.88) * mm, "end": v(31.5, 46.5) * mm});
            skLineSegment(sketch, "E129.2", {"start": v(31.5, 46.5) * mm, "end": v(19.5, 46.5) * mm});
            skLineSegment(sketch, "E129.3", {"start": v(19.5, 46.5) * mm, "end": v(13.5, 56.88) * mm});
            skLineSegment(sketch, "E129.4", {"start": v(13.5, 56.88) * mm, "end": v(19.5, 67.28) * mm});
            skLineSegment(sketch, "E129.5", {"start": v(19.5, 67.28) * mm, "end": v(31.5, 67.28) * mm});
            skPoint(sketch, "E129.0.midPoint", {"position": v(34.5, 62.08) * mm});
            skCircle(sketch, "E130.cCircle", {"center": v(25.5, 79.67) * mm, "radius": 10.4 * mm, "construction": true});
            skLineSegment(sketch, "E130.0", {"start": v(31.5, 90.06) * mm, "end": v(37.5, 79.67) * mm});
            skLineSegment(sketch, "E130.1", {"start": v(37.5, 79.67) * mm, "end": v(31.5, 69.28) * mm});
            skLineSegment(sketch, "E130.2", {"start": v(31.5, 69.28) * mm, "end": v(19.5, 69.28) * mm});
            skLineSegment(sketch, "E130.3", {"start": v(19.5, 69.28) * mm, "end": v(13.5, 79.67) * mm});
            skLineSegment(sketch, "E130.4", {"start": v(13.5, 79.67) * mm, "end": v(19.5, 90.06) * mm});
            skLineSegment(sketch, "E130.5", {"start": v(19.5, 90.06) * mm, "end": v(31.5, 90.06) * mm});
            skPoint(sketch, "E130.0.midPoint", {"position": v(34.5, 84.87) * mm});
            skCircle(sketch, "E131.cCircle", {"center": v(25.5, 102.45) * mm, "radius": 10.4 * mm, "construction": true});
            skLineSegment(sketch, "E131.0", {"start": v(31.5, 112.85) * mm, "end": v(37.5, 102.45) * mm});
            skLineSegment(sketch, "E131.1", {"start": v(37.5, 102.45) * mm, "end": v(31.5, 92.06) * mm});
            skLineSegment(sketch, "E131.2", {"start": v(31.5, 92.06) * mm, "end": v(19.5, 92.06) * mm});
            skLineSegment(sketch, "E131.3", {"start": v(19.5, 92.06) * mm, "end": v(13.5, 102.45) * mm});
            skLineSegment(sketch, "E131.4", {"start": v(13.5, 102.45) * mm, "end": v(19.5, 112.85) * mm});
            skLineSegment(sketch, "E131.5", {"start": v(19.5, 112.85) * mm, "end": v(31.5, 112.85) * mm});
            skPoint(sketch, "E131.0.midPoint", {"position": v(34.5, 107.65) * mm});
            skPoint(sketch, "E132.orphan", {"position": v(-8.23, -123.1) * mm});
            skPoint(sketch, "E133.orphan", {"position": v(17.77, -114) * mm});
            skPoint(sketch, "E134.orphan", {"position": v(-20.23, 125.53) * mm});
            skPoint(sketch, "E119.0.start.orphan", {"position": v(11.77, 124.24) * mm});
            skPoint(sketch, "E135.orphan", {"position": v(-6.23, 113.85) * mm});
            skPoint(sketch, "E136.orphan", {"position": v(-6.23, -114) * mm});
            skLineSegment(sketch, "E137", {"start": v(-5.65, -113) * mm, "end": v(17.2, -113) * mm});
            skPoint(sketch, "E138.orphan", {"position": v(17.77, 113.85) * mm});
            skLineSegment(sketch, "E139.trimOffspring", {"start": v(-5.65, 112.85) * mm, "end": v(17.2, 112.85) * mm});
            skSolve(sketch);
        }
        {
            var Q0;
            {Q0=qUnion([makeQuery(id+"F0.imprint","IMPRINT",FACE,{"disambiguationData":[TD([[makeQuery(id+"F0.imprint","IMPRINT",EDGE,{"derivedFrom":sQuery(id+"F0.wireOp",EDGE,"E7.bottom")}),-1.0]])]}),makeQuery(id+"F0.imprint","IMPRINT",FACE,{"disambiguationData":[TD([[makeQuery(id+"F0.imprint","IMPRINT",EDGE,{"derivedFrom":sQuery(id+"F0.wireOp",EDGE,"E15.bottom")}),-1.0]])]}),makeQuery(id+"F0.imprint","IMPRINT",FACE,{"disambiguationData":[TD([[makeQuery(id+"F0.imprint","IMPRINT",EDGE,{"derivedFrom":sQuery(id+"F0.wireOp",EDGE,"E16.bottom")}),-1.0]])]}),makeQuery(id+"F0.imprint","IMPRINT",FACE,{"disambiguationData":[TD([[makeQuery(id+"F0.imprint","IMPRINT",EDGE,{"derivedFrom":sQuery(id+"F0.wireOp",EDGE,"E20.bottom")}),-1.0]])]}),makeQuery(id+"F0.imprint","IMPRINT",FACE,{"disambiguationData":[TD([[makeQuery(id+"F0.imprint","IMPRINT",EDGE,{"derivedFrom":sQuery(id+"F0.wireOp",EDGE,"E25.bottom")}),-1.0]])]}),makeQuery(id+"F0.imprint","IMPRINT",FACE,{"disambiguationData":[TD([[makeQuery(id+"F0.imprint","IMPRINT",EDGE,{"derivedFrom":sQuery(id+"F0.wireOp",EDGE,"E17.bottom")}),-1.0]])]}),makeQuery(id+"F0.imprint","IMPRINT",FACE,{"disambiguationData":[TD([[makeQuery(id+"F0.imprint","IMPRINT",EDGE,{"derivedFrom":sQuery(id+"F0.wireOp",EDGE,"E18.bottom")}),-1.0]])]}),makeQuery(id+"F0.imprint","IMPRINT",FACE,{"disambiguationData":[TD([[makeQuery(id+"F0.imprint","IMPRINT",EDGE,{"derivedFrom":sQuery(id+"F0.wireOp",EDGE,"E10.bottom")}),-1.0]])]}),makeQuery(id+"F0.imprint","IMPRINT",FACE,{"disambiguationData":[TD([[makeQuery(id+"F0.imprint","IMPRINT",EDGE,{"derivedFrom":sQuery(id+"F0.wireOp",EDGE,"E22.bottom")}),-1.0]])]}),makeQuery(id+"F0.imprint","IMPRINT",FACE,{"disambiguationData":[TD([[makeQuery(id+"F0.imprint","IMPRINT",EDGE,{"derivedFrom":sQuery(id+"F0.wireOp",EDGE,"E21.bottom")}),-1.0]])]}),makeQuery(id+"F0.imprint","IMPRINT",FACE,{"disambiguationData":[TD([[makeQuery(id+"F0.imprint","IMPRINT",EDGE,{"derivedFrom":sQuery(id+"F0.wireOp",EDGE,"E11.bottom")}),-1.0]])]}),makeQuery(id+"F0.imprint","IMPRINT",FACE,{"disambiguationData":[TD([[makeQuery(id+"F0.imprint","IMPRINT",EDGE,{"derivedFrom":sQuery(id+"F0.wireOp",EDGE,"E13.bottom")}),-1.0]])]}),makeQuery(id+"F0.imprint","IMPRINT",FACE,{"disambiguationData":[TD([[makeQuery(id+"F0.imprint","IMPRINT",EDGE,{"derivedFrom":sQuery(id+"F0.wireOp",EDGE,"E19.bottom")}),-1.0]])]}),makeQuery(id+"F0.imprint","IMPRINT",FACE,{"disambiguationData":[TD([[makeQuery(id+"F0.imprint","IMPRINT",EDGE,{"derivedFrom":sQuery(id+"F0.wireOp",EDGE,"E12.bottom")}),-1.0]])]}),makeQuery(id+"F0.imprint","IMPRINT",FACE,{"disambiguationData":[TD([[makeQuery(id+"F0.imprint","IMPRINT",EDGE,{"derivedFrom":sQuery(id+"F0.wireOp",EDGE,"E27.bottom")}),-1.0]])]}),makeQuery(id+"F0.imprint","IMPRINT",FACE,{"disambiguationData":[TD([[makeQuery(id+"F0.imprint","IMPRINT",EDGE,{"derivedFrom":sQuery(id+"F0.wireOp",EDGE,"E26.bottom")}),-1.0]])]}),makeQuery(id+"F0.imprint","IMPRINT",FACE,{"disambiguationData":[TD([[makeQuery(id+"F0.imprint","IMPRINT",EDGE,{"derivedFrom":sQuery(id+"F0.wireOp",EDGE,"E8.bottom")}),-1.0]])]}),makeQuery(id+"F0.imprint","IMPRINT",FACE,{"disambiguationData":[TD([[makeQuery(id+"F0.imprint","IMPRINT",EDGE,{"derivedFrom":sQuery(id+"F0.wireOp",EDGE,"E14.bottom")}),-1.0]])]}),makeQuery(id+"F0.imprint","IMPRINT",FACE,{"disambiguationData":[TD([[makeQuery(id+"F0.imprint","IMPRINT",EDGE,{"derivedFrom":sQuery(id+"F0.wireOp",EDGE,"E4.bottom")}),-1.0]])]}),makeQuery(id+"F0.imprint","IMPRINT",FACE,{"disambiguationData":[TD([[makeQuery(id+"F0.imprint","IMPRINT",EDGE,{"derivedFrom":sQuery(id+"F0.wireOp",EDGE,"E23.bottom")}),-1.0]])]}),makeQuery(id+"F0.imprint","IMPRINT",FACE,{"disambiguationData":[TD([[makeQuery(id+"F0.imprint","IMPRINT",EDGE,{"derivedFrom":sQuery(id+"F0.wireOp",EDGE,"E0.bottom")}),-1.0]])]}),makeQuery(id+"F0.imprint","IMPRINT",FACE,{"disambiguationData":[TD([[makeQuery(id+"F0.imprint","IMPRINT",EDGE,{"derivedFrom":sQuery(id+"F0.wireOp",EDGE,"E24.bottom")}),-1.0]])]}),makeQuery(id+"F0.imprint","IMPRINT",FACE,{"disambiguationData":[TD([[makeQuery(id+"F0.imprint","IMPRINT",EDGE,{"derivedFrom":sQuery(id+"F0.wireOp",EDGE,"E5.bottom")}),-1.0]])]}),makeQuery(id+"F0.imprint","IMPRINT",FACE,{"disambiguationData":[TD([[makeQuery(id+"F0.imprint","IMPRINT",EDGE,{"derivedFrom":sQuery(id+"F0.wireOp",EDGE,"E9.bottom")}),-1.0]])]}),makeQuery(id+"F0.imprint","IMPRINT",FACE,{"disambiguationData":[TD([[makeQuery(id+"F0.imprint","IMPRINT",EDGE,{"derivedFrom":sQuery(id+"F0.wireOp",EDGE,"E6.bottom")}),-1.0]])]})]);}
            extrude(context, id + "F2", {"entities" : qUnion([Q0]), "depth" : 2 * mm, "offsetDistance" : 25 * mm});
        }
        {
            var Q0;
            Q0 = qSketchRegion(id + "F1", true);
            extrude(context, id + "F3", {"entities" : qUnion([Q0]), "operationType" : NewBodyOperationType.REMOVE, "endBound" : BoundingType.SYMMETRIC, "oppositeDirection" : true, "depth" : 25 * mm, "offsetDistance" : 25 * mm});
        }
    });
